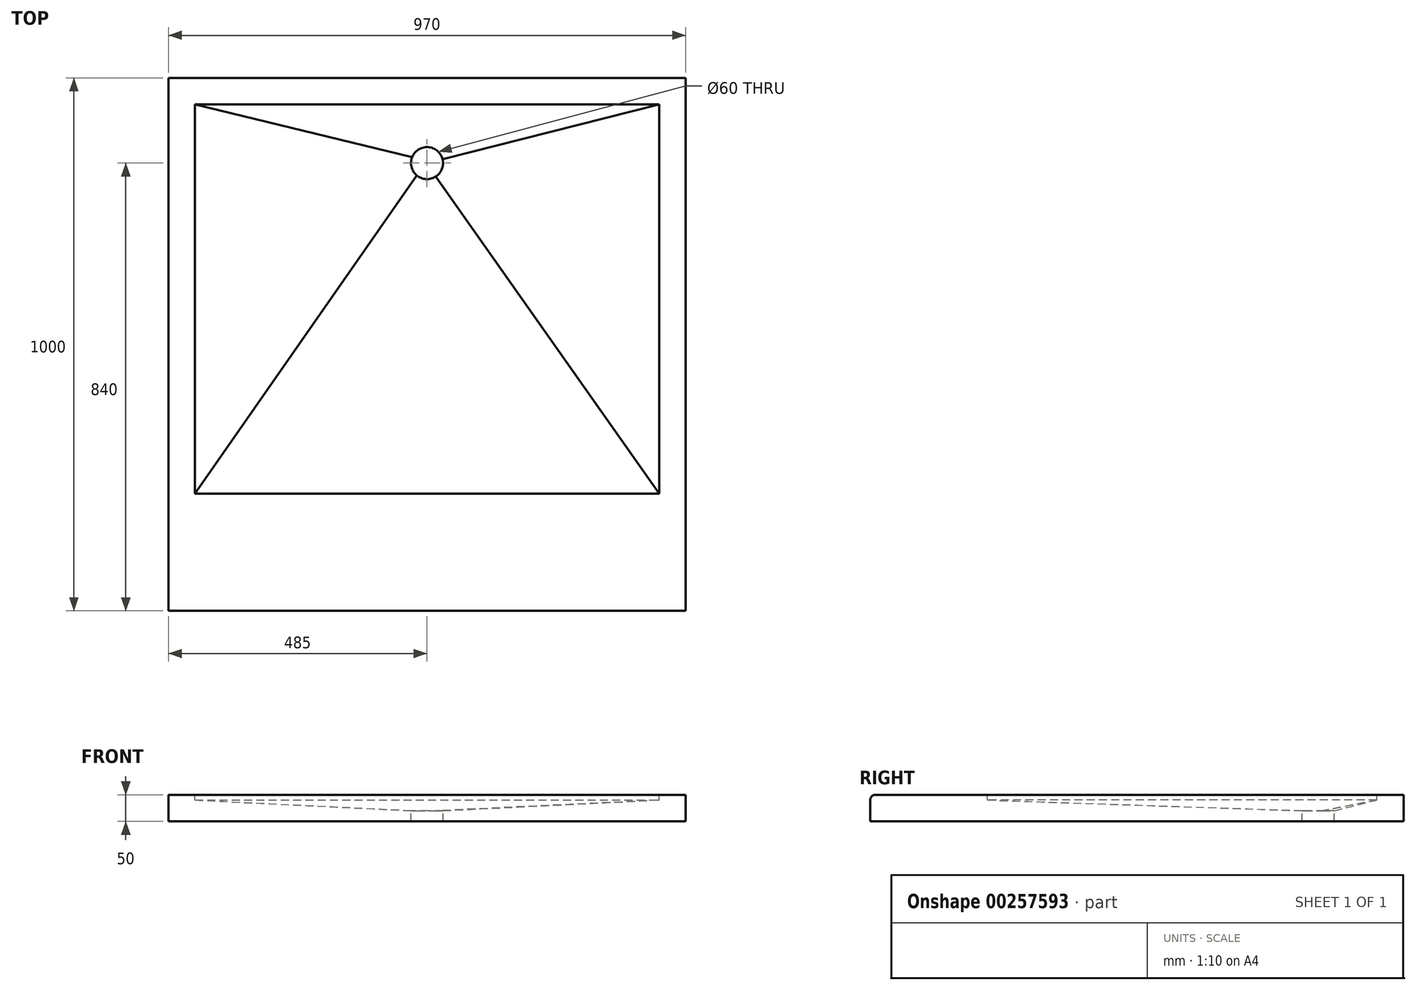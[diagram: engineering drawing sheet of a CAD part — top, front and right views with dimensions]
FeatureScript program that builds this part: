
annotation { "Feature Type Name" : "Feature", "Feature Type Description" : "" }
export const myFeature = defineFeature(function(context is Context, id is Id, definition is map)
    precondition{}
    {
        {
            var Q0;
            Q0=qCreatedBy(makeId("Top.planeOp"),FACE);
            var sketch = newSketch(context, id + "F0", { "sketchPlane" : qUnion([Q0])});
            skLineSegment(sketch, "E0.bottom", {"start": v(485, -500) * mm, "end": v(-485, -500) * mm});
            skLineSegment(sketch, "E0.top", {"start": v(485, 500) * mm, "end": v(-485, 500) * mm});
            skLineSegment(sketch, "E0.left", {"start": v(485, -500) * mm, "end": v(485, 500) * mm});
            skLineSegment(sketch, "E0.right", {"start": v(-485, -500) * mm, "end": v(-485, 500) * mm});
            skPoint(sketch, "E0.middle", {"position": v(0, 0) * mm});
            skSolve(sketch);
        }
        {
            var Q0;
            Q0 = qSketchRegion(id + "F0", true);
            extrude(context, id + "F1", {"entities" : qUnion([Q0]), "depth" : 50 * mm});
        }
        {
            var Q0;
            Q0=makeQuery(id+"F1.opExtrude","CAP_FACE",FACE,{"disambiguationData":[OSD([sQuery(id+"F0.wireOp",EDGE,"E0.bottom"),sQuery(id+"F0.wireOp",EDGE,"E0.top"),sQuery(id+"F0.wireOp",EDGE,"E0.left"),sQuery(id+"F0.wireOp",EDGE,"E0.right")])],"isStart":false});
            var sketch = newSketch(context, id + "F2", { "sketchPlane" : qUnion([Q0])});
            skLineSegment(sketch, "E1.bottom", {"start": v(-435, 450) * mm, "end": v(435, 450) * mm});
            skLineSegment(sketch, "E1.top", {"start": v(-435, -280) * mm, "end": v(435, -280) * mm});
            skLineSegment(sketch, "E1.left", {"start": v(-435, 450) * mm, "end": v(-435, -280) * mm});
            skLineSegment(sketch, "E1.right", {"start": v(435, 450) * mm, "end": v(435, -280) * mm});
            skLineSegment(sketch, "E2", {"start": v(0, 500) * mm, "end": v(0, 340) * mm, "construction": true});
            skSolve(sketch);
        }
        {
            var Q0;
            Q0=qCreatedBy(makeId("Top.planeOp"),FACE);
            cPlane(context, id + "F3", {"entities" : qUnion([Q0]), "cplaneType" : CPlaneType.OFFSET, "offset" : 20 * mm, "width" : 150 * mm, "height" : 150 * mm});
        }
        {
            var Q0;
            Q0=qCreatedBy(id+"F3.planeOp",FACE);
            var sketch = newSketch(context, id + "F4", { "sketchPlane" : qUnion([Q0])});
            skLineSegment(sketch, "E3.0", {"start": v(0, 500) * mm, "end": v(0, 340) * mm, "construction": true});
            skCircle(sketch, "E4", {"center": v(0, 340) * mm, "radius": 30 * mm});
            skSolve(sketch);
        }
        {
            var Q0;
            Q0=makeQuery(id+"F2.imprint","IMPRINT",FACE,{"disambiguationData":[TD([[makeQuery(id+"F2.imprint","IMPRINT",EDGE,{"derivedFrom":sQuery(id+"F2.wireOp",EDGE,"E1.bottom")}),-1.0]])]});
            extrude(context, id + "F5", {"entities" : qUnion([Q0]), "operationType" : NewBodyOperationType.REMOVE, "oppositeDirection" : true, "depth" : 10 * mm});
        }
        {
            var Q0;
            Q0=makeQuery(id+"F1.opExtrude","CAP_FACE",FACE,{"disambiguationData":[OSD([sQuery(id+"F0.wireOp",EDGE,"E0.bottom"),sQuery(id+"F0.wireOp",EDGE,"E0.top"),sQuery(id+"F0.wireOp",EDGE,"E0.left"),sQuery(id+"F0.wireOp",EDGE,"E0.right")])],"isStart":false});
            var sketch = newSketch(context, id + "F6", { "sketchPlane" : qUnion([Q0])});
            skLineSegment(sketch, "E5", {"start": v(0, 450) * mm, "end": v(0, 340) * mm, "construction": true});
            skLineSegment(sketch, "E6", {"start": v(435, 349.38) * mm, "end": v(28.5, 349.38) * mm, "construction": true});
            skLineSegment(sketch, "E7.0", {"start": v(0, 500) * mm, "end": v(0, 340) * mm});
            skCircle(sketch, "E7.1", {"center": v(0, 340) * mm, "radius": 30 * mm});
            skLineSegment(sketch, "E8.trimOffspring", {"start": v(-28.5, 349.38) * mm, "end": v(-435, 349.38) * mm, "construction": true});
            skLineSegment(sketch, "E9.trimOffspring", {"start": v(0, 310) * mm, "end": v(0, -280) * mm, "construction": true});
            skSolve(sketch);
        }
        {
            var Q0;
            Q0=makeQuery(id+"F5.boolean.opBoolean","COPY",VERTEX,{"derivedFrom":makeQuery(id+"F5.opExtrude","CAP_VERTEX",VERTEX,{"disambiguationData":[OSD([sQuery(id+"F2.wireOp",EDGE,"E1.top"),sQuery(id+"F2.wireOp",EDGE,"E1.right")])],"isStart":true})});
            var Q1;
            {var subQ0=sQuery(id+"F2.wireOp",EDGE,"E1.right");var subQ1=sQuery(id+"F2.wireOp",EDGE,"E1.top");Q1=makeQuery(id+"FYE2c4HLsG9rWFW_1.boolean.opBoolean","MERGE",VERTEX,{"derivedFrom":[makeQuery(id+"F5.boolean.opBoolean","COPY",VERTEX,{"derivedFrom":makeQuery(id+"F5.opExtrude","CAP_VERTEX",VERTEX,{"disambiguationData":[OSD([subQ1,subQ0])],"isStart":false})}),makeQuery(id+"FYE2c4HLsG9rWFW_1.opLoft","MID_CAP_VERTEX",VERTEX,{"disambiguationData":[OSD([subQ1,subQ0])],"capPos":0.0})]});}
            var Q2;
            Q2=sQuery(id+"F6.wireOp",VERTEX,"E5.end");
            cPlane(context, id + "F7", {"entities" : qUnion([Q0, Q1, Q2]), "cplaneType" : CPlaneType.THREE_POINT, "offset" : 25 * mm, "width" : 150 * mm, "height" : 150 * mm});
        }
        {
            var Q0;
            Q0=qCreatedBy(id+"F7.planeOp",FACE);
            var sketch = newSketch(context, id + "F8", { "sketchPlane" : qUnion([Q0])});
            skLineSegment(sketch, "E10", {"start": v(479.05, 40) * mm, "end": v(-278.33, 20) * mm});
            skSolve(sketch);
        }
        {
            var Q0;
            Q0=makeQuery(id+"F5.boolean.opBoolean","COPY",VERTEX,{"derivedFrom":makeQuery(id+"F5.opExtrude","CAP_VERTEX",VERTEX,{"disambiguationData":[OSD([sQuery(id+"F2.wireOp",EDGE,"E1.top"),sQuery(id+"F2.wireOp",EDGE,"E1.left")])],"isStart":true})});
            var Q1;
            Q1=makeQuery(id+"F5.boolean.opBoolean","COPY",VERTEX,{"derivedFrom":makeQuery(id+"F5.opExtrude","CAP_VERTEX",VERTEX,{"disambiguationData":[OSD([sQuery(id+"F2.wireOp",EDGE,"E1.top"),sQuery(id+"F2.wireOp",EDGE,"E1.left")])],"isStart":false})});
            var Q2;
            Q2=sQuery(id+"F4.wireOp",VERTEX,"E4.center");
            cPlane(context, id + "F9", {"entities" : qUnion([Q0, Q1, Q2]), "cplaneType" : CPlaneType.THREE_POINT, "offset" : 25 * mm, "width" : 150 * mm, "height" : 150 * mm});
        }
        {
            var Q0;
            Q0=qCreatedBy(id+"F9.planeOp",FACE);
            var sketch = newSketch(context, id + "F10", { "sketchPlane" : qUnion([Q0])});
            skLineSegment(sketch, "E11", {"start": v(-278.33, 20) * mm, "end": v(479.05, 40) * mm});
            skSolve(sketch);
        }
        {
            var Q0;
            Q0=sQuery(id+"F8.wireOp",VERTEX,"E10.start");
            var Q1;
            Q1=sQuery(id+"F10.wireOp",VERTEX,"E11.end");
            var Q2;
            Q2=makeQuery(id+"F5.boolean.opBoolean","COPY",VERTEX,{"derivedFrom":makeQuery(id+"F5.opExtrude","CAP_VERTEX",VERTEX,{"disambiguationData":[OSD([sQuery(id+"F2.wireOp",EDGE,"E1.bottom"),sQuery(id+"F2.wireOp",EDGE,"E1.left")])],"isStart":false})});
            cPlane(context, id + "F11", {"entities" : qUnion([Q0, Q1, Q2]), "cplaneType" : CPlaneType.THREE_POINT, "offset" : 25 * mm, "width" : 150 * mm, "height" : 150 * mm});
        }
        {
            var Q0;
            Q0=qCreatedBy(id+"F11.planeOp",FACE);
            var sketch = newSketch(context, id + "F12", { "sketchPlane" : qUnion([Q0])});
            skLineSegment(sketch, "E12.0.0", {"start": v(435, 450) * mm, "end": v(0, 450) * mm});
            skLineSegment(sketch, "E12.0.1", {"start": v(0, 450) * mm, "end": v(-435, 450) * mm});
            skLineSegment(sketch, "E12.0.2", {"start": v(-435, 450) * mm, "end": v(-435, -280) * mm});
            skLineSegment(sketch, "E12.0.3", {"start": v(-435, -280) * mm, "end": v(435, -280) * mm});
            skLineSegment(sketch, "E12.0.4", {"start": v(435, -280) * mm, "end": v(435, 450) * mm});
            skSolve(sketch);
        }
        {
            var Q1;
            Q1 = qSketchRegion(id + "F12", true);
            var Q2;
            Q2 = qSketchRegion(id + "F4", true);
            loft(context, id + "F13", {"operationType" : NewBodyOperationType.REMOVE, "sheetProfilesArray" : [{ "sheetProfileEntities" : qUnion([Q1]) }, { "sheetProfileEntities" : qUnion([Q2]) }]});
        }
        {
            var Q0;
            Q0 = qSketchRegion(id + "F4", true);
            extrude(context, id + "F14", {"entities" : qUnion([Q0]), "operationType" : NewBodyOperationType.REMOVE, "oppositeDirection" : true, "depth" : 25 * mm});
        }
        {
            var Q0;
            Q0=makeQuery(id+"F5.boolean.opBoolean","COPY",EDGE,{"derivedFrom":makeQuery(id+"F5.opExtrude","CAP_EDGE",EDGE,{"disambiguationData":[OSD([sQuery(id+"F2.wireOp",EDGE,"E1.left")])],"isStart":true})});
            var Q1;
            Q1=makeQuery(id+"F5.boolean.opBoolean","COPY",EDGE,{"derivedFrom":makeQuery(id+"F5.opExtrude","CAP_EDGE",EDGE,{"disambiguationData":[OSD([sQuery(id+"F2.wireOp",EDGE,"E1.bottom")])],"isStart":true})});
            var Q2;
            Q2=makeQuery(id+"F5.boolean.opBoolean","COPY",EDGE,{"derivedFrom":makeQuery(id+"F5.opExtrude","CAP_EDGE",EDGE,{"disambiguationData":[OSD([sQuery(id+"F2.wireOp",EDGE,"E1.right")])],"isStart":true})});
            var Q3;
            Q3=makeQuery(id+"F5.boolean.opBoolean","COPY",EDGE,{"derivedFrom":makeQuery(id+"F5.opExtrude","CAP_EDGE",EDGE,{"disambiguationData":[OSD([sQuery(id+"F2.wireOp",EDGE,"E1.top")])],"isStart":true})});
            var Q4;
            Q4=makeQuery(id+"F1.opExtrude","CAP_EDGE",EDGE,{"disambiguationData":[OSD([sQuery(id+"F0.wireOp",EDGE,"E0.bottom")])],"isStart":false});
            fillet(context, id + "F15", {"entities" : qUnion([Q0, Q1, Q2, Q3, Q4]), "radius" : 10 * mm, "tangentPropagation" : true, "allowEdgeOverflow" : false});
        }
    });
